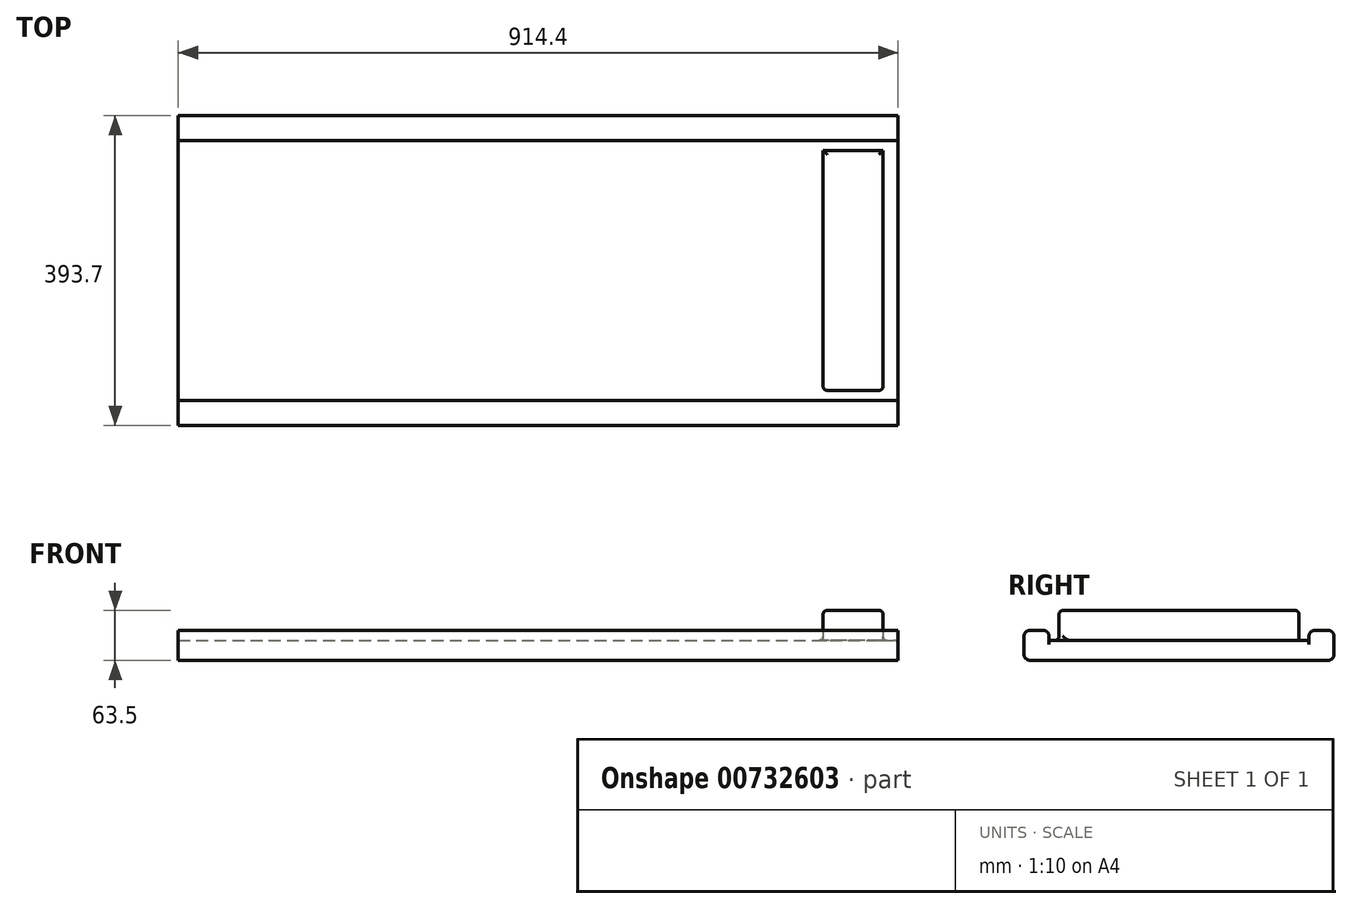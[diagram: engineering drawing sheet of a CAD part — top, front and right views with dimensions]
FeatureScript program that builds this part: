
annotation { "Feature Type Name" : "Feature", "Feature Type Description" : "" }
export const myFeature = defineFeature(function(context is Context, id is Id, definition is map)
    precondition{}
    {
        {
            var Q0;
            Q0=qCreatedBy(makeId("Top.planeOp"),FACE);
            var sketch = newSketch(context, id + "F0", { "sketchPlane" : qUnion([Q0])});
            skLineSegment(sketch, "E0.bottom", {"start": v(0, 0) * mm, "end": v(914.4, 0) * mm});
            skLineSegment(sketch, "E0.top", {"start": v(0, 393.7) * mm, "end": v(914.4, 393.7) * mm});
            skLineSegment(sketch, "E0.left", {"start": v(0, 0) * mm, "end": v(0, 393.7) * mm});
            skLineSegment(sketch, "E0.right", {"start": v(914.4, 0) * mm, "end": v(914.4, 393.7) * mm});
            skSolve(sketch);
        }
        {
            var Q0;
            Q0 = qSketchRegion(id + "F0", true);
            extrude(context, id + "F1", {"entities" : qUnion([Q0]), "depth" : 25.4 * mm, "offsetDistance" : 25.4 * mm});
        }
        {
            var Q0;
            Q0=makeQuery(id+"F1.opExtrude","CAP_FACE",FACE,{"disambiguationData":[OSD([sQuery(id+"F0.wireOp",EDGE,"E0.bottom"),sQuery(id+"F0.wireOp",EDGE,"E0.top"),sQuery(id+"F0.wireOp",EDGE,"E0.left"),sQuery(id+"F0.wireOp",EDGE,"E0.right")])],"isStart":false});
            var sketch = newSketch(context, id + "F2", { "sketchPlane" : qUnion([Q0])});
            skLineSegment(sketch, "E1.bottom", {"start": v(914.4, 393.7) * mm, "end": v(0, 393.7) * mm});
            skLineSegment(sketch, "E1.top", {"start": v(914.4, 361.95) * mm, "end": v(0, 361.95) * mm});
            skLineSegment(sketch, "E1.left", {"start": v(914.4, 393.7) * mm, "end": v(914.4, 361.95) * mm});
            skLineSegment(sketch, "E1.right", {"start": v(0, 393.7) * mm, "end": v(0, 361.95) * mm});
            skLineSegment(sketch, "E2.bottom", {"start": v(0, 0) * mm, "end": v(914.4, 0) * mm});
            skLineSegment(sketch, "E2.top", {"start": v(0, 31.75) * mm, "end": v(914.4, 31.75) * mm});
            skLineSegment(sketch, "E2.left", {"start": v(0, 0) * mm, "end": v(0, 31.75) * mm});
            skLineSegment(sketch, "E2.right", {"start": v(914.4, 0) * mm, "end": v(914.4, 31.75) * mm});
            skSolve(sketch);
        }
        {
            var Q0;
            Q0 = qSketchRegion(id + "F2", true);
            extrude(context, id + "F3", {"entities" : qUnion([Q0]), "operationType" : NewBodyOperationType.ADD, "depth" : 12.7 * mm, "offsetDistance" : 25.4 * mm});
        }
        {
            var Q0;
            Q0=makeQuery(id+"F1.opExtrude","CAP_FACE",FACE,{"disambiguationData":[OSD([sQuery(id+"F0.wireOp",EDGE,"E0.bottom"),sQuery(id+"F0.wireOp",EDGE,"E0.top"),sQuery(id+"F0.wireOp",EDGE,"E0.left"),sQuery(id+"F0.wireOp",EDGE,"E0.right")])],"isStart":false});
            var sketch = newSketch(context, id + "F4", { "sketchPlane" : qUnion([Q0])});
            skLineSegment(sketch, "E3.bottom", {"start": v(895.35, 349.25) * mm, "end": v(819.15, 349.25) * mm});
            skLineSegment(sketch, "E3.top", {"start": v(895.35, 44.45) * mm, "end": v(819.15, 44.45) * mm});
            skLineSegment(sketch, "E3.left", {"start": v(895.35, 349.25) * mm, "end": v(895.35, 44.45) * mm});
            skLineSegment(sketch, "E3.right", {"start": v(819.15, 349.25) * mm, "end": v(819.15, 44.45) * mm});
            skSolve(sketch);
        }
        {
            var Q0;
            Q0 = qSketchRegion(id + "F4", true);
            extrude(context, id + "F5", {"entities" : qUnion([Q0]), "operationType" : NewBodyOperationType.ADD, "depth" : 38.1 * mm, "offsetDistance" : 25.4 * mm});
        }
        {
            var Q0;
            Q0=makeQuery(id+"F3.opExtrude","CAP_EDGE",EDGE,{"disambiguationData":[OSD([sQuery(id+"F2.wireOp",EDGE,"E1.bottom")])],"isStart":false});
            var Q1;
            Q1=makeQuery(id+"F3.opExtrude","CAP_EDGE",EDGE,{"disambiguationData":[OSD([sQuery(id+"F2.wireOp",EDGE,"E1.top")])],"isStart":false});
            var Q2;
            Q2=makeQuery(id+"F3.opExtrude","CAP_EDGE",EDGE,{"disambiguationData":[OSD([sQuery(id+"F2.wireOp",EDGE,"E2.top")])],"isStart":false});
            var Q3;
            Q3=makeQuery(id+"F3.opExtrude","CAP_EDGE",EDGE,{"disambiguationData":[OSD([sQuery(id+"F2.wireOp",EDGE,"E2.bottom")])],"isStart":false});
            var Q4;
            Q4=makeQuery(id+"F1.opExtrude","CAP_EDGE",EDGE,{"disambiguationData":[OSD([sQuery(id+"F0.wireOp",EDGE,"E0.top")])],"isStart":true});
            var Q5;
            Q5=makeQuery(id+"F1.opExtrude","CAP_EDGE",EDGE,{"disambiguationData":[OSD([sQuery(id+"F0.wireOp",EDGE,"E0.bottom")])],"isStart":true});
            fillet(context, id + "F6", {"entities" : qUnion([Q0, Q1, Q2, Q3, Q4, Q5]), "radius" : 7.62 * mm, "tangentPropagation" : true, "allowEdgeOverflow" : false});
        }
        {
            var Q0;
            Q0=makeQuery(id+"F5.opExtrude","CAP_FACE",FACE,{"disambiguationData":[OSD([sQuery(id+"F4.wireOp",EDGE,"E3.bottom"),sQuery(id+"F4.wireOp",EDGE,"E3.top"),sQuery(id+"F4.wireOp",EDGE,"E3.left"),sQuery(id+"F4.wireOp",EDGE,"E3.right")])],"isStart":false});
            var Q1;
            Q1=makeQuery(id+"F5.opExtrude","SWEPT_FACE",FACE,{"disambiguationData":[OSD([sQuery(id+"F4.wireOp",EDGE,"E3.top")])]});
            var Q2;
            Q2=makeQuery(id+"F3.opExtrude","CAP_EDGE",EDGE,{"disambiguationData":[OSD([sQuery(id+"F2.wireOp",EDGE,"E2.top")])],"isStart":true});
            var Q3;
            Q3=makeQuery(id+"F3.opExtrude","CAP_EDGE",EDGE,{"disambiguationData":[OSD([sQuery(id+"F2.wireOp",EDGE,"E1.top")])],"isStart":true});
            var Q4;
            Q4=makeQuery(id+"F1.opExtrude","CAP_EDGE",EDGE,{"disambiguationData":[OSD([sQuery(id+"F0.wireOp",EDGE,"E0.right")])],"isStart":false});
            fillet(context, id + "F7", {"entities" : qUnion([Q0, Q1, Q2, Q3, Q4]), "radius" : 5.08 * mm, "tangentPropagation" : true, "allowEdgeOverflow" : false});
        }
    });
